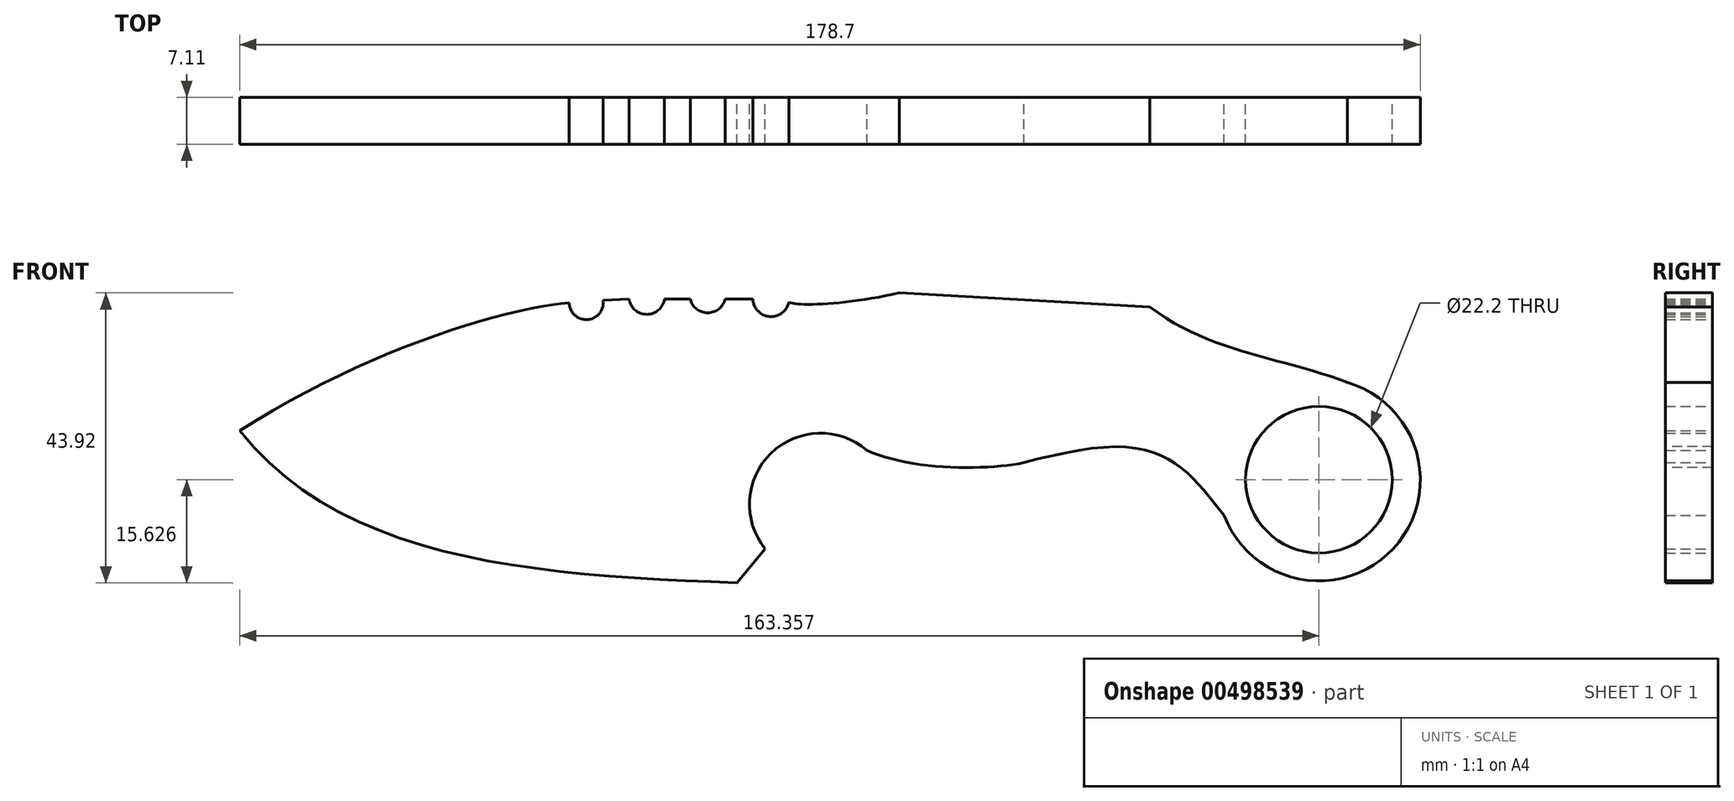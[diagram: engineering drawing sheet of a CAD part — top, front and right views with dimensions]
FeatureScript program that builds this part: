
annotation { "Feature Type Name" : "Feature", "Feature Type Description" : "" }
export const myFeature = defineFeature(function(context is Context, id is Id, definition is map)
    precondition{}
    {
        {
            var Q0;
            Q0=qCreatedBy(makeId("Front.planeOp"),FACE);
            var sketch = newSketch(context, id + "F0", { "sketchPlane" : qUnion([Q0])});
            skArc(sketch, "E0", {"start": v(-34.34, 43.95) * mm, "mid": v(-31.84, 41.26) * mm, "end": v(-28.92, 43.49) * mm});
            skPoint(sketch, "E0.first.point", {"position": v(-31.65, 41.25) * mm});
            skPoint(sketch, "E0.third.point", {"position": v(-34.34, 43.95) * mm});
            skArc(sketch, "E1", {"start": v(-43.85, 43.95) * mm, "mid": v(-41.2, 41.84) * mm, "end": v(-38.54, 43.95) * mm});
            skPoint(sketch, "E1.first.point", {"position": v(-38.54, 43.95) * mm});
            skPoint(sketch, "E1.second.point", {"position": v(-41.31, 41.84) * mm});
            skPoint(sketch, "E1.third.point", {"position": v(-43.85, 43.95) * mm});
            skArc(sketch, "E2", {"start": v(-53.1, 43.95) * mm, "mid": v(-50.42, 41.6) * mm, "end": v(-47.74, 43.95) * mm});
            skPoint(sketch, "E2.first.point", {"position": v(-47.74, 43.95) * mm});
            skPoint(sketch, "E2.second.point", {"position": v(-50.5, 41.6) * mm});
            skPoint(sketch, "E2.third.point", {"position": v(-53.1, 43.95) * mm});
            skArc(sketch, "E3", {"start": v(-62.16, 43.33) * mm, "mid": v(-59.36, 40.82) * mm, "end": v(-57.02, 43.76) * mm});
            skPoint(sketch, "E3.first.point", {"position": v(-57.02, 43.76) * mm});
            skPoint(sketch, "E3.second.point", {"position": v(-59.84, 40.82) * mm});
            skPoint(sketch, "E3.third.point", {"position": v(-62.16, 43.33) * mm});
            skArc(sketch, "E4", {"start": v(36.97, 11.15) * mm, "mid": v(62.58, 6.16) * mm, "end": v(55.61, 31.3) * mm});
            skPoint(sketch, "E4.first.point", {"position": v(36.97, 11.15) * mm});
            skPoint(sketch, "E4.second.point", {"position": v(65.62, 22.12) * mm});
            skPoint(sketch, "E4.third.point", {"position": v(55.61, 31.3) * mm});
            skFitSpline(sketch, "E5", {"points": [v(25.74, 42.73) * mm, v(55.61, 31.3) * mm], "startDerivative": vector(26.63, -20.55) * mm, "endDerivative": vector(29.88, -11.45) * mm});
            skFitSpline(sketch, "E6", {"points": [v(-10.99, 45.16) * mm, v(-28.92, 43.49) * mm, v(-28.88, 43.81) * mm, v(-28.9, 44.25) * mm], "startDerivative": vector(-33, -8.5) * mm, "endDerivative": vector(-0.55, 3.71) * mm});
            skLineSegment(sketch, "E7", {"start": v(-34.34, 43.95) * mm, "end": v(-38.54, 43.95) * mm});
            skLineSegment(sketch, "E8", {"start": v(-57.02, 43.76) * mm, "end": v(-53.1, 43.95) * mm});
            skLineSegment(sketch, "E9", {"start": v(-47.74, 43.95) * mm, "end": v(-43.85, 43.95) * mm});
            skCircle(sketch, "E10", {"center": v(51.32, 16.58) * mm, "radius": 11.1 * mm});
            skFitSpline(sketch, "E11", {"points": [v(36.97, 11.15) * mm, v(20.82, 21.55) * mm, v(-20.74, 12.33) * mm, v(-28.9, 21.79) * mm], "startDerivative": vector(-40.37, 50.71) * mm, "endDerivative": vector(-113.03, 42.92) * mm});
            skFitSpline(sketch, "E12", {"points": [v(6.66, 19.15) * mm, v(-19.69, 22.65) * mm, v(-20.7, 37.6) * mm], "startDerivative": vector(-34.96, -7.6) * mm, "endDerivative": vector(7.05, 40.98) * mm});
            skArc(sketch, "E13", {"start": v(-17.1, 21) * mm, "mid": v(-31.61, 20.57) * mm, "end": v(-32.49, 6.07) * mm});
            skPoint(sketch, "E13.second.point", {"position": v(-28.43, 2.98) * mm});
            skPoint(sketch, "E13.third.point", {"position": v(-21.34, 2.44) * mm});
            skLineSegment(sketch, "E14", {"start": v(-32.49, 6.07) * mm, "end": v(-36.79, 0.95) * mm});
            skFitSpline(sketch, "E15", {"points": [v(-36.79, 0.95) * mm, v(-112.04, 23.98) * mm], "startDerivative": vector(-89.85, 3.52) * mm, "endDerivative": vector(-48.12, 60.28) * mm});
            skFitSpline(sketch, "E16", {"points": [v(-112.04, 23.98) * mm, v(-62.16, 43.33) * mm, v(-55.81, 40.82) * mm], "startDerivative": vector(77.75, 49.91) * mm, "endDerivative": vector(13.76, -25.1) * mm});
            skLineSegment(sketch, "E17", {"start": v(25.74, 42.73) * mm, "end": v(-12.19, 44.87) * mm});
            skSolve(sketch);
        }
        {
            var Q0;
            Q0=makeQuery(id+"F0.imprint","IMPRINT",FACE,{"disambiguationData":[TD([[makeQuery(id+"F0.imprint","IMPRINT",EDGE,{"derivedFrom":sQuery(id+"F0.wireOp",EDGE,"E0")}),-1.0]])]});
            extrude(context, id + "F1", {"entities" : qUnion([Q0]), "depth" : 7.11 * mm});
        }
    });
